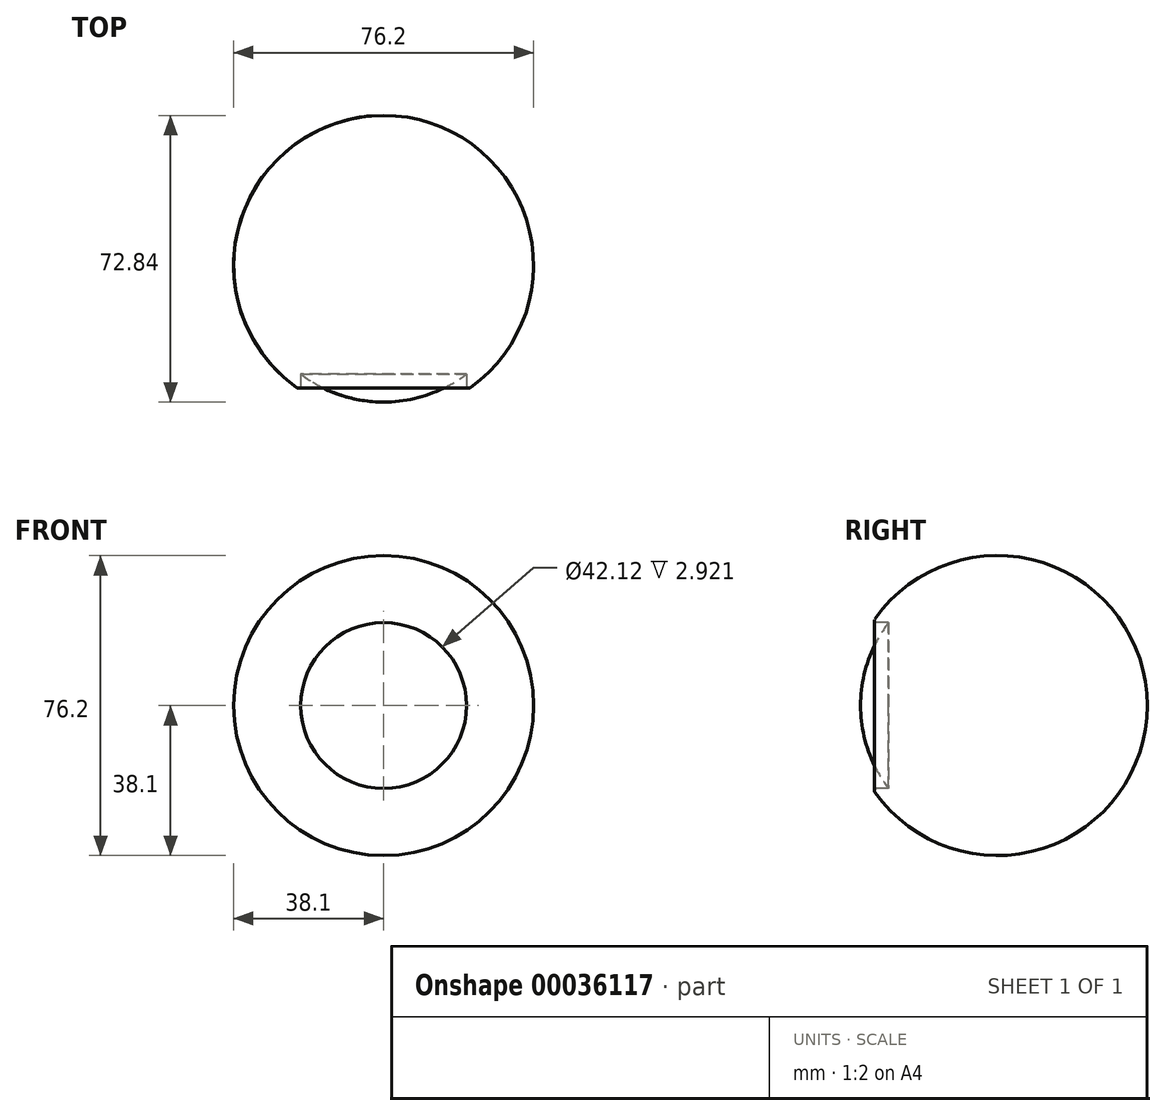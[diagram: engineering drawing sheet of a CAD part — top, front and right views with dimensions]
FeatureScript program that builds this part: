
annotation { "Feature Type Name" : "Feature", "Feature Type Description" : "" }
export const myFeature = defineFeature(function(context is Context, id is Id, definition is map)
    precondition{}
    {
        {
            var Q0;
            Q0=qCreatedBy(makeId("Top.planeOp"),FACE);
            var sketch = newSketch(context, id + "F0", { "sketchPlane" : qUnion([Q0])});
            skCircle(sketch, "E0", {"center": v(0, 0) * mm, "radius": 38.1 * mm});
            skLineSegment(sketch, "E1", {"start": v(0, 0) * mm, "end": v(0, 38.1) * mm});
            skLineSegment(sketch, "E2", {"start": v(0, 0) * mm, "end": v(0, -38.1) * mm});
            skSolve(sketch);
        }
        {
            var Q0;
            {var subQ0=sQuery(id+"F0.wireOp",EDGE,"E1");Q0=makeQuery(id+"F0.imprint","IMPRINT",FACE,{"disambiguationData":[TD([[makeQuery(id+"F0.imprint","IMPRINT",EDGE,{"derivedFrom":subQ0}),-1.0]])]});}
            var Q1;
            Q1=sQuery(id+"F0.wireOp",EDGE,"E1");
            revolve(context, id + "F1", {"entities" : qUnion([Q0]), "axis" : qUnion([Q1]), "revolveType" : RevolveType.FULL});
        }
        {
            var Q0;
            Q0=qCreatedBy(makeId("Front.planeOp"),FACE);
            cPlane(context, id + "F2", {"entities" : qUnion([Q0]), "cplaneType" : CPlaneType.OFFSET, "offset" : 31.75 * mm, "width" : 152.4 * mm, "height" : 152.4 * mm});
        }
        {
            var Q0;
            Q0=qCreatedBy(id+"F2.planeOp",FACE);
            var sketch = newSketch(context, id + "F3", { "sketchPlane" : qUnion([Q0])});
            skCircle(sketch, "E3", {"center": v(0, 0) * mm, "radius": 21.17 * mm});
            skSolve(sketch);
        }
        {
            var Q0;
            Q0=makeQuery(id+"F3.imprint","IMPRINT",FACE,{"disambiguationData":[TD([[makeQuery(id+"F3.imprint","IMPRINT",EDGE,{"derivedFrom":sQuery(id+"F3.wireOp",EDGE,"E3")}),1.0]])]});
            extrude(context, id + "F4", {"entities" : qUnion([Q0]), "operationType" : NewBodyOperationType.REMOVE, "depth" : 25.4 * mm});
        }
        {
            var Q0;
            Q0=makeQuery(id+"F4.boolean.opBoolean","COPY",FACE,{"derivedFrom":makeQuery(id+"F4.opExtrude","CAP_FACE",FACE,{"disambiguationData":[OSD([sQuery(id+"F3.wireOp",EDGE,"E3")])],"isStart":true})});
            extrude(context, id + "F5", {"entities" : qUnion([Q0]), "operationType" : NewBodyOperationType.REMOVE, "oppositeDirection" : true, "depth" : 4.13 * mm});
        }
        {
            var Q0;
            {var subQ0=sQuery(id+"F3.wireOp",EDGE,"E3");var subQ1=sQuery(id+"F0.wireOp",EDGE,"E0");Q0=makeQuery(id+"F5.boolean.opBoolean","MERGE",EDGE,{"derivedFrom":[makeQuery(id+"F4.boolean.opBoolean","INTERSECT",EDGE,{"derivedFrom":[makeQuery(id+"F1.opRevolve","SWEPT_FACE",FACE,{"disambiguationData":[OSD([subQ1])]}),makeQuery(id+"F4.opExtrude","CAP_FACE",FACE,{"disambiguationData":[OSD([subQ0])],"isStart":true})]}),makeQuery(id+"F5.opExtrude","CAP_EDGE",EDGE,{"disambiguationData":[OSD([subQ1,subQ0])],"isStart":true})]});}
            fillet(context, id + "F6", {"entities" : qUnion([Q0]), "radius" : 0.64 * mm, "tangentPropagation" : true, "allowEdgeOverflow" : false});
        }
        {
            var Q0;
            Q0=qCreatedBy(makeId("Top.planeOp"),FACE);
            var sketch = newSketch(context, id + "F7", { "sketchPlane" : qUnion([Q0])});
            skLineSegment(sketch, "E4.0", {"start": v(-21.06, -27.62) * mm, "end": v(21.06, -27.62) * mm});
            skCircle(sketch, "E5", {"center": v(0, 0) * mm, "radius": 34.74 * mm});
            skLineSegment(sketch, "E6", {"start": v(0, -27.62) * mm, "end": v(0, -34.74) * mm});
            skPoint(sketch, "E6.endSnap0", {"position": v(0, -32.8) * mm});
            skSolve(sketch);
        }
        {
            var Q0;
            {var subQ3=sQuery(id+"F7.wireOp",EDGE,"E6");Q0=makeQuery(id+"F7.imprint","IMPRINT",FACE,{"disambiguationData":[TD([[makeQuery(id+"F7.imprint","IMPRINT",EDGE,{"derivedFrom":subQ3}),-1.0]])]});}
            var Q1;
            Q1=sQuery(id+"F7.wireOp",EDGE,"E6");
            revolve(context, id + "F8", {"entities" : qUnion([Q0]), "axis" : qUnion([Q1]), "revolveType" : RevolveType.FULL});
        }
    });
